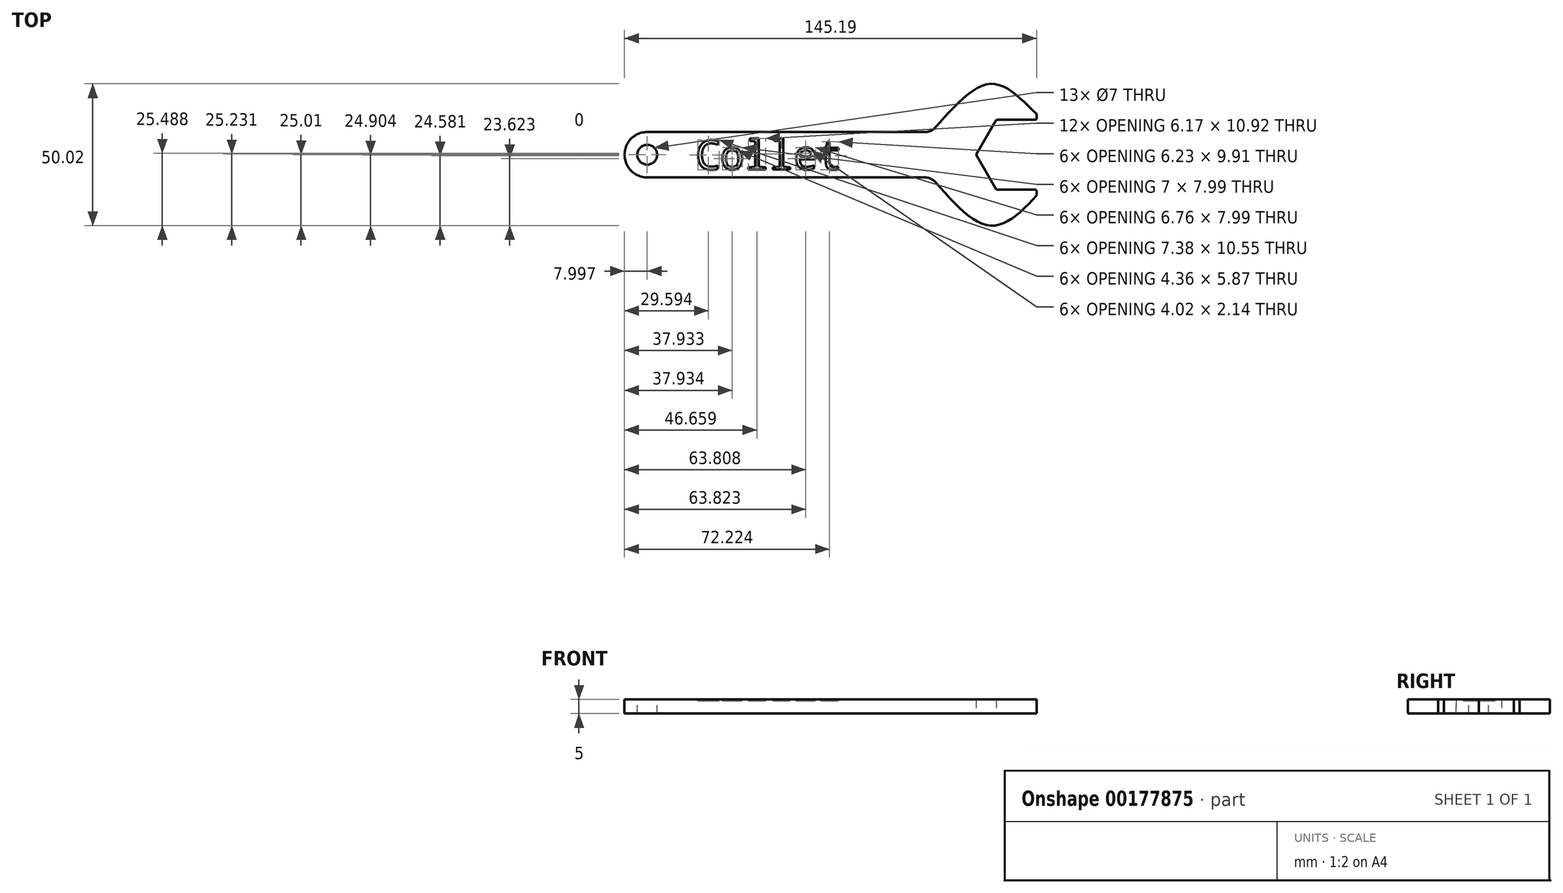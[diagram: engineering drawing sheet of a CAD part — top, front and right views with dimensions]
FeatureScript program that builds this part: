
annotation { "Feature Type Name" : "Feature", "Feature Type Description" : "" }
export const myFeature = defineFeature(function(context is Context, id is Id, definition is map)
    precondition{}
    {
        {
            var Q0;
            Q0=qCreatedBy(makeId("Top.planeOp"),FACE);
            var sketch = newSketch(context, id + "F0", { "sketchPlane" : qUnion([Q0])});
            skCircle(sketch, "E0.cCircle", {"center": v(0, 0) * mm, "radius": 12.32 * mm, "construction": true});
            skLineSegment(sketch, "E0.0", {"start": v(-7.12, 12.32) * mm, "end": v(7.12, 12.32) * mm});
            skLineSegment(sketch, "E0.1", {"start": v(7.12, 12.32) * mm, "end": v(14.23, 0) * mm});
            skLineSegment(sketch, "E0.2", {"start": v(14.23, 0) * mm, "end": v(7.12, -12.32) * mm});
            skLineSegment(sketch, "E0.3", {"start": v(7.12, -12.32) * mm, "end": v(-7.12, -12.33) * mm});
            skLineSegment(sketch, "E0.4", {"start": v(-7.12, -12.33) * mm, "end": v(-14.23, 0) * mm});
            skLineSegment(sketch, "E0.5", {"start": v(-14.23, 0) * mm, "end": v(-7.12, 12.32) * mm});
            skPoint(sketch, "E0.0.midPoint", {"position": v(0, 12.32) * mm});
            skLineSegment(sketch, "E1.bottom", {"start": v(-30, 8) * mm, "end": v(-30, 8) * mm});
            skLineSegment(sketch, "E1.top", {"start": v(-30, -8) * mm, "end": v(-30, -8) * mm});
            skLineSegment(sketch, "E1.left", {"start": v(-30, 8) * mm, "end": v(-30, -8) * mm});
            skLineSegment(sketch, "E1.right", {"start": v(-30, 8) * mm, "end": v(-30, -8) * mm});
            skLineSegment(sketch, "E2.bottom", {"start": v(-130, 8) * mm, "end": v(-30, 8) * mm});
            skLineSegment(sketch, "E2.top", {"start": v(-130, -8) * mm, "end": v(-30, -8) * mm});
            skLineSegment(sketch, "E2.left", {"start": v(-130, 8) * mm, "end": v(-130, -8) * mm});
            skCircle(sketch, "E3", {"center": v(-130.07, 0) * mm, "radius": 8 * mm});
            skPoint(sketch, "E3.third.point", {"position": v(-136.8, 4.32) * mm});
            skLineSegment(sketch, "E4", {"start": v(7.12, 12.32) * mm, "end": v(7.12, 14.32) * mm});
            skLineSegment(sketch, "E5", {"start": v(7.12, -12.32) * mm, "end": v(7.12, -14.32) * mm});
            skFitSpline(sketch, "E6", {"points": [v(7.12, 14.32) * mm, v(-9, 25) * mm, v(-30, 8) * mm], "startDerivative": vector(-34.01, 32.77) * mm, "endDerivative": vector(-40.04, -43.18) * mm});
            skFitSpline(sketch, "E7", {"points": [v(7.12, -14.32) * mm, v(-9, -25) * mm, v(-30, -8) * mm], "startDerivative": vector(-32.7, -36.93) * mm, "endDerivative": vector(-41.26, 46.88) * mm});
            skSolve(sketch);
        }
        {
            var Q0;
            {var subQ3=sQuery(id+"F0.wireOp",EDGE,"E2.bottom");Q0=makeQuery(id+"F0.imprint","IMPRINT",FACE,{"disambiguationData":[TD([[makeQuery(id+"F0.imprint","IMPRINT",EDGE,{"derivedFrom":subQ3}),-1.0]])]});}
            var Q1;
            {var subQ0=sQuery(id+"F0.wireOp",EDGE,"E2.left");Q1=makeQuery(id+"F0.imprint","IMPRINT",FACE,{"disambiguationData":[TD([[makeQuery(id+"F0.imprint","IMPRINT",EDGE,{"derivedFrom":subQ0}),1.0]])]});}
            var Q2;
            {var subQ0=sQuery(id+"F0.wireOp",EDGE,"E2.left");Q2=makeQuery(id+"F0.imprint","IMPRINT",FACE,{"disambiguationData":[TD([[makeQuery(id+"F0.imprint","IMPRINT",EDGE,{"derivedFrom":subQ0}),-1.0]])]});}
            var Q3;
            Q3=makeQuery(id+"F0.imprint","IMPRINT",FACE,{"disambiguationData":[TD([[makeQuery(id+"F0.imprint","IMPRINT",EDGE,{"derivedFrom":sQuery(id+"F0.wireOp",EDGE,"E0.0")}),1.0]])]});
            extrude(context, id + "F1", {"entities" : qUnion([Q0, Q1, Q2, Q3]), "depth" : 5 * mm});
        }
        {
            var Q0;
            Q0=makeQuery(id+"F1.opExtrude","CAP_FACE",FACE,{"disambiguationData":[OSD([sQuery(id+"F0.wireOp",EDGE,"E0.0"),sQuery(id+"F0.wireOp",EDGE,"E0.3"),sQuery(id+"F0.wireOp",EDGE,"E0.4"),sQuery(id+"F0.wireOp",EDGE,"E0.5"),sQuery(id+"F0.wireOp",EDGE,"8e9e9b65-ac2f-468e-a00c-45cfab599eec"),sQuery(id+"F0.wireOp",EDGE,"dbf11928-1581-4c0f-8f04-2778a1c86a44"),sQuery(id+"F0.wireOp",EDGE,"E2.bottom"),sQuery(id+"F0.wireOp",EDGE,"E2.top"),sQuery(id+"F0.wireOp",EDGE,"E1.left"),sQuery(id+"F0.wireOp",EDGE,"E3")])],"isStart":false});
            var sketch = newSketch(context, id + "F2", { "sketchPlane" : qUnion([Q0])});
            skCircle(sketch, "E8", {"center": v(-130.07, 0) * mm, "radius": 3.5 * mm});
            skSolve(sketch);
        }
        {
            var Q0;
            Q0=makeQuery(id+"F2.imprint","IMPRINT",FACE,{"disambiguationData":[TD([[makeQuery(id+"F2.imprint","IMPRINT",EDGE,{"derivedFrom":sQuery(id+"F2.wireOp",EDGE,"E8")}),1.0]])]});
            extrude(context, id + "F3", {"entities" : qUnion([Q0]), "operationType" : NewBodyOperationType.REMOVE, "oppositeDirection" : true, "depth" : 25 * mm});
        }
        {
            var Q0;
            Q0=makeQuery(id+"F1.opExtrude","CAP_FACE",FACE,{"disambiguationData":[OSD([sQuery(id+"F0.wireOp",EDGE,"E0.0"),sQuery(id+"F0.wireOp",EDGE,"E0.3"),sQuery(id+"F0.wireOp",EDGE,"E0.4"),sQuery(id+"F0.wireOp",EDGE,"E0.5"),sQuery(id+"F0.wireOp",EDGE,"8e9e9b65-ac2f-468e-a00c-45cfab599eec"),sQuery(id+"F0.wireOp",EDGE,"dbf11928-1581-4c0f-8f04-2778a1c86a44"),sQuery(id+"F0.wireOp",EDGE,"E2.bottom"),sQuery(id+"F0.wireOp",EDGE,"E2.top"),sQuery(id+"F0.wireOp",EDGE,"E1.left"),sQuery(id+"F0.wireOp",EDGE,"E3")])],"isStart":false});
            var sketch = newSketch(context, id + "F4", { "sketchPlane" : qUnion([Q0])});
            skText(sketch, "E9", { "text": "Collet", "fontName": "DroidSansMono.ttf"});
            const initialGuessF4  = {"E9": [-0.11307, -0.00524, 1, 0, 0.01035]};
            skSetInitialGuess(sketch, initialGuessF4);
            skSolve(sketch);
        }
        {
            var Q0;
            Q0 = qSketchRegion(id + "F4", true);
            extrude(context, id + "F5", {"entities" : qUnion([Q0]), "operationType" : NewBodyOperationType.REMOVE, "oppositeDirection" : true, "depth" : .5 * mm});
        }
        {
            var Q0;
            Q0=makeQuery(id+"F1.opExtrude","SWEPT_EDGE",EDGE,{"disambiguationData":[OSD([sQuery(id+"F0.wireOp",EDGE,"8e9e9b65-ac2f-468e-a00c-45cfab599eec"),sQuery(id+"F0.wireOp",EDGE,"E2.bottom"),sQuery(id+"F0.wireOp",EDGE,"E1.left")])]});
            var Q1;
            Q1=makeQuery(id+"F1.opExtrude","SWEPT_EDGE",EDGE,{"disambiguationData":[OSD([sQuery(id+"F0.wireOp",EDGE,"dbf11928-1581-4c0f-8f04-2778a1c86a44"),sQuery(id+"F0.wireOp",EDGE,"E2.top"),sQuery(id+"F0.wireOp",EDGE,"E1.left")])]});
            fillet(context, id + "F6", {"entities" : qUnion([Q0, Q1]), "radius" : 5 * mm, "tangentPropagation" : true, "allowEdgeOverflow" : false});
        }
        {
            var Q0;
            Q0=makeQuery(id+"F1.opExtrude","SWEPT_EDGE",EDGE,{"disambiguationData":[OSD([sQuery(id+"F0.wireOp",EDGE,"E0.2"),sQuery(id+"F0.wireOp",EDGE,"E0.3"),sQuery(id+"F0.wireOp",EDGE,"dbf11928-1581-4c0f-8f04-2778a1c86a44")])]});
            var Q1;
            Q1=makeQuery(id+"F1.opExtrude","SWEPT_EDGE",EDGE,{"disambiguationData":[OSD([sQuery(id+"F0.wireOp",EDGE,"E0.0"),sQuery(id+"F0.wireOp",EDGE,"E0.1"),sQuery(id+"F0.wireOp",EDGE,"8e9e9b65-ac2f-468e-a00c-45cfab599eec")])]});
            fillet(context, id + "F7", {"entities" : qUnion([Q0, Q1]), "radius" : .5 * mm, "tangentPropagation" : true, "allowEdgeOverflow" : false});
        }
    });
